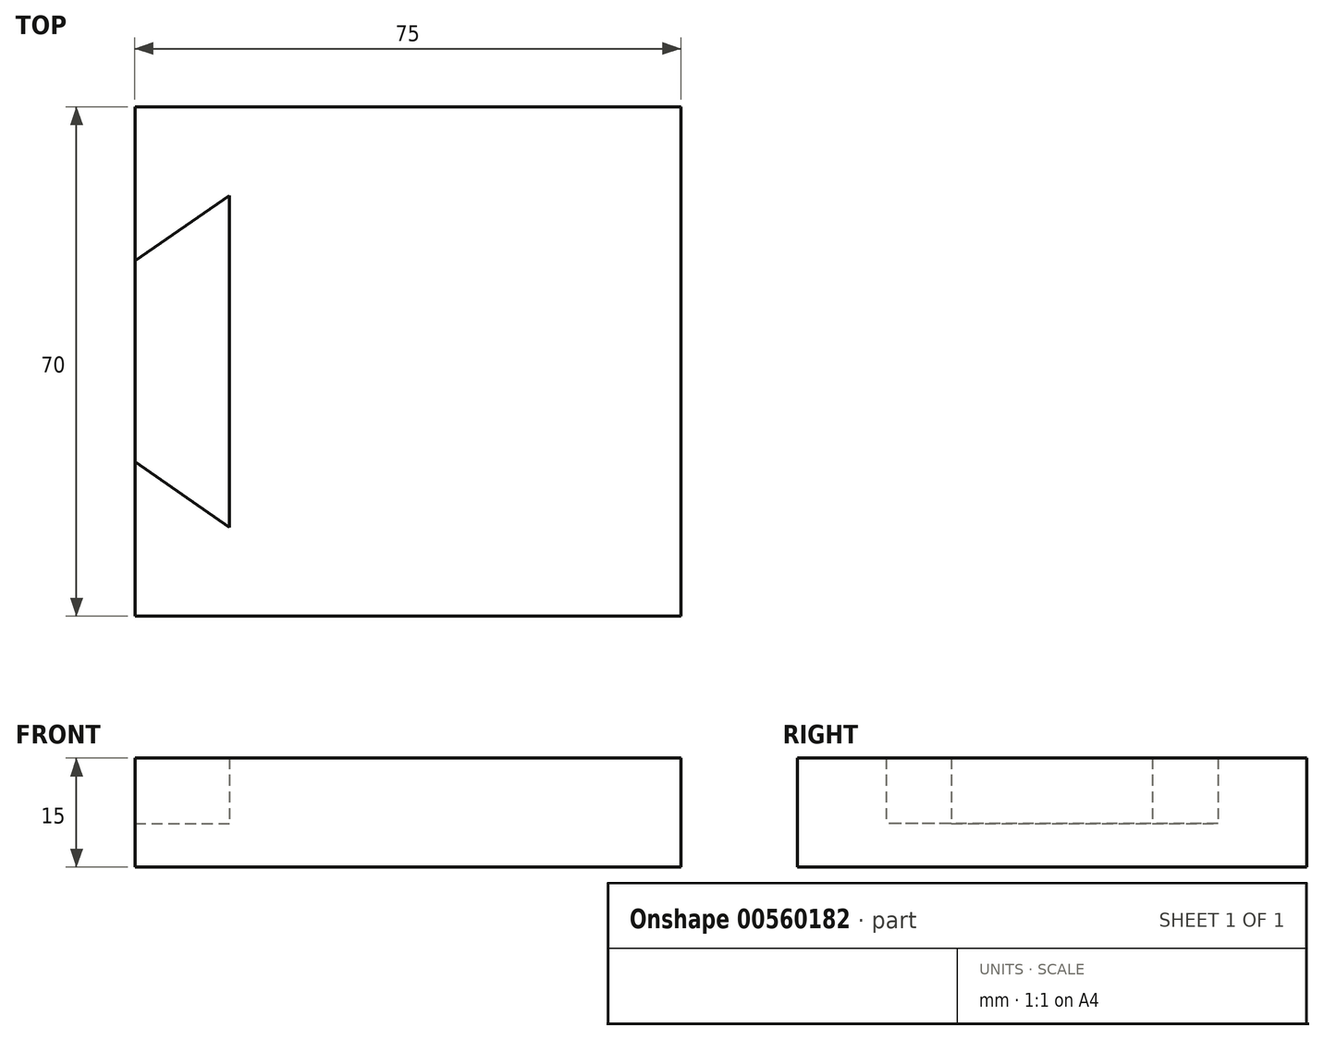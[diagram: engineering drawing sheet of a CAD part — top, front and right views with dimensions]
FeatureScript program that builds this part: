
annotation { "Feature Type Name" : "Feature", "Feature Type Description" : "" }
export const myFeature = defineFeature(function(context is Context, id is Id, definition is map)
    precondition{}
    {
        {
            var Q0;
            Q0=qCreatedBy(makeId("Top.planeOp"),FACE);
            var sketch = newSketch(context, id + "F0", { "sketchPlane" : qUnion([Q0])});
            skLineSegment(sketch, "E0.bottom", {"start": v(-73.2, 32.5) * mm, "end": v(76.8, 32.5) * mm});
            skLineSegment(sketch, "E0.top", {"start": v(-73.2, -37.5) * mm, "end": v(76.8, -37.5) * mm});
            skLineSegment(sketch, "E0.left", {"start": v(-73.2, 32.5) * mm, "end": v(-73.2, -37.5) * mm});
            skLineSegment(sketch, "E0.right", {"start": v(76.8, 32.5) * mm, "end": v(76.8, -37.5) * mm});
            skPoint(sketch, "E0.middle", {"position": v(1.8, -2.5) * mm});
            skLineSegment(sketch, "E1", {"start": v(1.8, 32.5) * mm, "end": v(1.8, 11.31) * mm});
            skPoint(sketch, "E1.endSnap0", {"position": v(1.8, 32.5) * mm});
            skLineSegment(sketch, "E2", {"start": v(1.8, 11.31) * mm, "end": v(14.78, 20.3) * mm});
            skLineSegment(sketch, "E3", {"start": v(14.78, 20.3) * mm, "end": v(14.78, -2.5) * mm});
            skLineSegment(sketch, "E4", {"start": v(-87.4, -2.5) * mm, "end": v(112.64, -2.5) * mm, "construction": true});
            skPoint(sketch, "E4.endSnap0", {"position": v(-73.2, -2.5) * mm});
            skLineSegment(sketch, "E5.MirrorCS", {"start": v(14.78, -25.3) * mm, "end": v(14.78, -2.5) * mm});
            skLineSegment(sketch, "E6.MirrorCS", {"start": v(1.8, -16.31) * mm, "end": v(14.78, -25.3) * mm});
            skLineSegment(sketch, "E7.MirrorCS", {"start": v(1.8, -37.5) * mm, "end": v(1.8, -16.31) * mm});
            skSolve(sketch);
        }
        {
            var Q0;
            {var subQ0=sQuery(id+"F0.wireOp",EDGE,"E0.right");Q0=makeQuery(id+"F0.imprint","IMPRINT",FACE,{"disambiguationData":[TD([[makeQuery(id+"F0.imprint","IMPRINT",EDGE,{"derivedFrom":subQ0}),-1.0]])]});}
            extrude(context, id + "F1", {"entities" : qUnion([Q0]), "depth" : 15 * mm, "offsetDistance" : 25 * mm});
        }
        {
            var Q0;
            Q0=makeQuery(id+"F1.opExtrude","SWEPT_FACE",FACE,{"disambiguationData":[OSD([sQuery(id+"F0.wireOp",EDGE,"E0.right")])]});
            var sketch = newSketch(context, id + "F2", { "sketchPlane" : qUnion([Q0])});
            skLineSegment(sketch, "E8.bottom", {"start": v(52.79, -9.06) * mm, "end": v(-83.41, -9.06) * mm});
            skLineSegment(sketch, "E8.top", {"start": v(52.79, 6) * mm, "end": v(-83.41, 6) * mm});
            skLineSegment(sketch, "E8.left", {"start": v(52.79, -9.06) * mm, "end": v(52.79, 6) * mm});
            skLineSegment(sketch, "E8.right", {"start": v(-83.41, -9.06) * mm, "end": v(-83.41, 6) * mm});
            skSolve(sketch);
        }
        {
            var Q0;
            {var subQ1=sQuery(id+"F0.wireOp",EDGE,"E0.right");var subQ6=makeQuery(id+"F1.opExtrude","CAP_EDGE",EDGE,{"disambiguationData":[OSD([subQ1])],"isStart":true});Q0=makeQuery(id+"F2.imprint","IMPRINT",FACE,{"disambiguationData":[TD([[makeQuery(id+"F2.imprint","IMPRINT",EDGE,{"derivedFrom":subQ6}),-1.0]])]});}
            var Q1;
            Q1=makeQuery(id+"F1.opExtrude","SWEPT_FACE",FACE,{"disambiguationData":[OSD([sQuery(id+"F0.wireOp",EDGE,"E1")])]});
            extrude(context, id + "F3", {"entities" : qUnion([Q0]), "operationType" : NewBodyOperationType.ADD, "endBound" : BoundingType.UP_TO_SURFACE, "oppositeDirection" : true, "depth" : 25 * mm, "endBoundEntityFace" : qUnion([Q1]), "offsetDistance" : 25 * mm});
        }
    });
